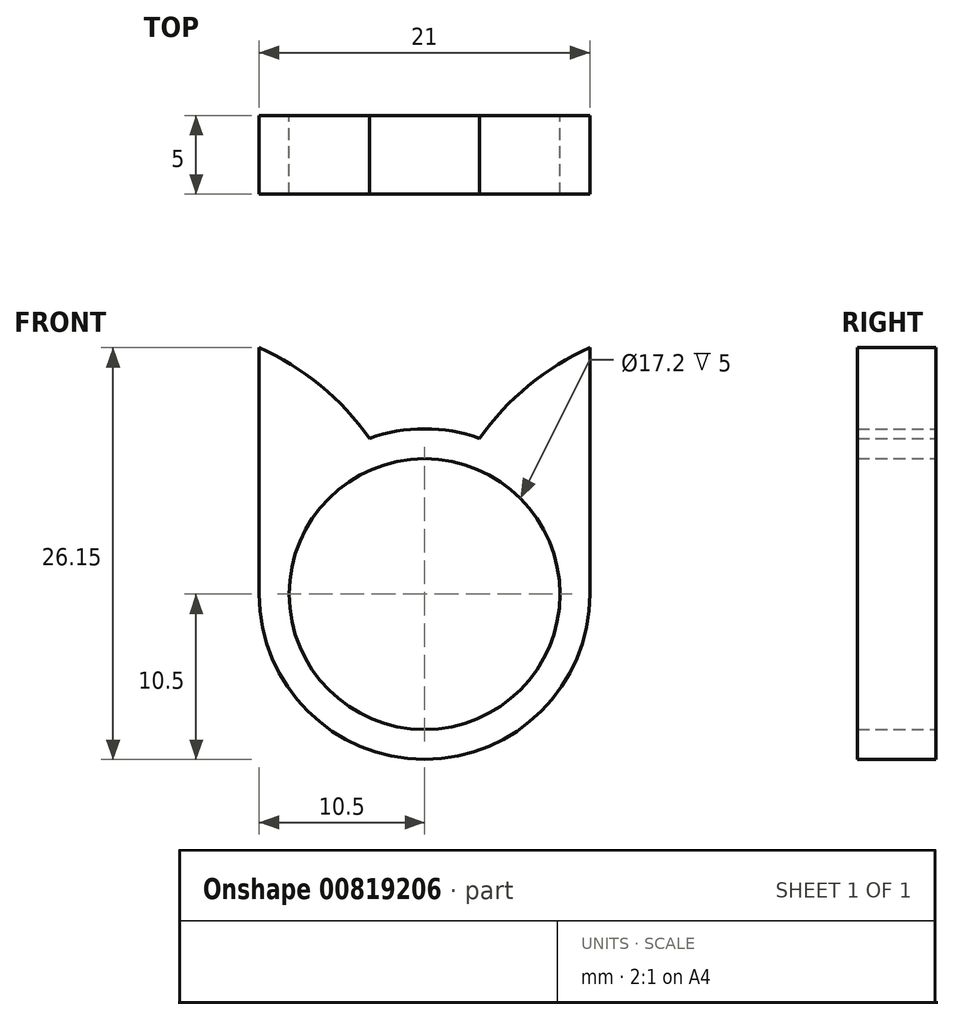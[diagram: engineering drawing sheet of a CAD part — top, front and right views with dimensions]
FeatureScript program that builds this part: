
annotation { "Feature Type Name" : "Feature", "Feature Type Description" : "" }
export const myFeature = defineFeature(function(context is Context, id is Id, definition is map)
    precondition{}
    {
        {
            var Q0;
            Q0=qCreatedBy(makeId("Front.planeOp"),FACE);
            var sketch = newSketch(context, id + "F0", { "sketchPlane" : qUnion([Q0])});
            skArc(sketch, "E0", {"start": v(-10.5, 0) * mm, "mid": v(0, -10.5) * mm, "end": v(10.5, 0) * mm});
            skCircle(sketch, "E1", {"center": v(0, 0) * mm, "radius": 8.6 * mm});
            skLineSegment(sketch, "E2", {"start": v(-10.5, 0) * mm, "end": v(-10.5, 15.65) * mm});
            skArc(sketch, "E3", {"start": v(-3.5, 9.9) * mm, "mid": v(-6.61, 13.25) * mm, "end": v(-10.5, 15.65) * mm});
            skArc(sketch, "E4.MirrorCS", {"start": v(3.5, 9.9) * mm, "mid": v(6.61, 13.25) * mm, "end": v(10.5, 15.65) * mm});
            skLineSegment(sketch, "E5.MirrorCS", {"start": v(10.5, 0) * mm, "end": v(10.5, 15.65) * mm});
            skArc(sketch, "E6.trimOffspring", {"start": v(3.5, 9.9) * mm, "mid": v(0, 10.5) * mm, "end": v(-3.5, 9.9) * mm});
            skSolve(sketch);
        }
        {
            var Q0;
            Q0=makeQuery(id+"F0.imprint","IMPRINT",FACE,{"disambiguationData":[TD([[makeQuery(id+"F0.imprint","IMPRINT",EDGE,{"derivedFrom":sQuery(id+"F0.wireOp",EDGE,"E0")}),1.0]])]});
            extrude(context, id + "F1", {"entities" : qUnion([Q0]), "depth" : 5 * mm, "offsetDistance" : 25 * mm});
        }
    });
